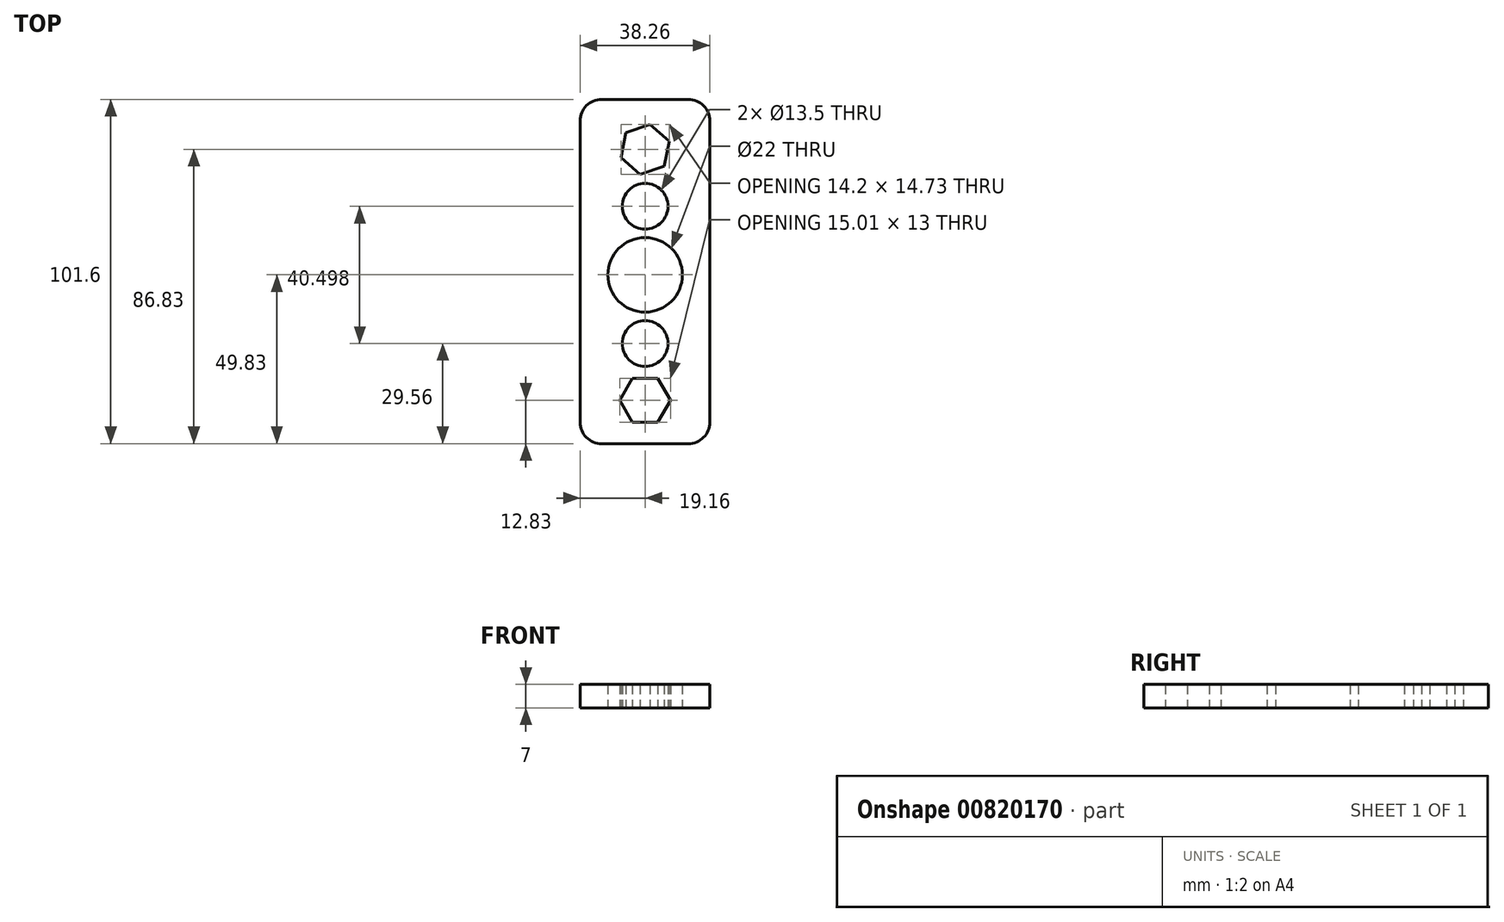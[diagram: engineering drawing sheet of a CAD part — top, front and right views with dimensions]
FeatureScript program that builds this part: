
annotation { "Feature Type Name" : "Feature", "Feature Type Description" : "" }
export const myFeature = defineFeature(function(context is Context, id is Id, definition is map)
    precondition{}
    {
        {
            var Q0;
            Q0=qCreatedBy(makeId("Top.planeOp"),FACE);
            var sketch = newSketch(context, id + "F0", { "sketchPlane" : qUnion([Q0])});
            skCircle(sketch, "E0", {"center": v(0, 0) * mm, "radius": 11 * mm});
            skLineSegment(sketch, "E1.bottom", {"start": v(-12.81, 51.77) * mm, "end": v(12.75, 51.77) * mm});
            skLineSegment(sketch, "E1.top", {"start": v(-12.81, -49.83) * mm, "end": v(12.75, -49.83) * mm});
            skLineSegment(sketch, "E1.left", {"start": v(-19.16, 45.42) * mm, "end": v(-19.16, -43.48) * mm});
            skLineSegment(sketch, "E1.right", {"start": v(19.1, 45.42) * mm, "end": v(19.1, -43.48) * mm});
            skPoint(sketch, "E2.visualSharp", {"position": v(-19.16, 51.77) * mm});
            skArc(sketch, "E2.filletArc", {"start": v(-12.81, 51.77) * mm, "mid": v(-17.3, 49.9) * mm, "end": v(-19.16, 45.42) * mm});
            skPoint(sketch, "E3.visualSharp", {"position": v(19.1, 51.77) * mm});
            skArc(sketch, "E3.filletArc", {"start": v(19.1, 45.42) * mm, "mid": v(17.24, 49.9) * mm, "end": v(12.75, 51.77) * mm});
            skPoint(sketch, "E4.visualSharp", {"position": v(19.1, -49.83) * mm});
            skArc(sketch, "E4.filletArc", {"start": v(12.75, -49.83) * mm, "mid": v(17.24, -47.97) * mm, "end": v(19.1, -43.48) * mm});
            skPoint(sketch, "E5.visualSharp", {"position": v(-19.16, -49.83) * mm});
            skArc(sketch, "E5.filletArc", {"start": v(-19.16, -43.48) * mm, "mid": v(-17.3, -47.97) * mm, "end": v(-12.81, -49.83) * mm});
            skCircle(sketch, "E6.cCircle", {"center": v(0, 37) * mm, "radius": 6.5 * mm, "construction": true});
            skLineSegment(sketch, "E6.0", {"start": v(7.1, 39.43) * mm, "end": v(5.66, 32.07) * mm});
            skLineSegment(sketch, "E6.1", {"start": v(5.66, 32.07) * mm, "end": v(-1.44, 29.63) * mm});
            skLineSegment(sketch, "E6.2", {"start": v(-1.44, 29.63) * mm, "end": v(-7.1, 34.57) * mm});
            skLineSegment(sketch, "E6.3", {"start": v(-7.1, 34.57) * mm, "end": v(-5.66, 41.93) * mm});
            skLineSegment(sketch, "E6.4", {"start": v(-5.66, 41.93) * mm, "end": v(1.44, 44.37) * mm});
            skLineSegment(sketch, "E6.5", {"start": v(1.44, 44.37) * mm, "end": v(7.1, 39.43) * mm});
            skPoint(sketch, "E6.0.midPoint", {"position": v(6.38, 35.75) * mm});
            skCircle(sketch, "E7.cCircle", {"center": v(0, -37) * mm, "radius": 6.5 * mm, "construction": true});
            skLineSegment(sketch, "E7.0", {"start": v(3.75, -43.5) * mm, "end": v(-3.75, -43.5) * mm});
            skLineSegment(sketch, "E7.1", {"start": v(-3.75, -43.5) * mm, "end": v(-7.5, -37) * mm});
            skLineSegment(sketch, "E7.2", {"start": v(-7.5, -37) * mm, "end": v(-3.75, -30.5) * mm});
            skLineSegment(sketch, "E7.3", {"start": v(-3.75, -30.5) * mm, "end": v(3.75, -30.5) * mm});
            skLineSegment(sketch, "E7.4", {"start": v(3.75, -30.5) * mm, "end": v(7.5, -37) * mm});
            skLineSegment(sketch, "E7.5", {"start": v(7.5, -37) * mm, "end": v(3.75, -43.5) * mm});
            skPoint(sketch, "E7.0.midPoint", {"position": v(0, -43.5) * mm});
            skCircle(sketch, "E8", {"center": v(0, -20.27) * mm, "radius": 6.75 * mm});
            skCircle(sketch, "E9", {"center": v(0, 20.23) * mm, "radius": 6.75 * mm});
            skSolve(sketch);
        }
        {
            var Q0;
            Q0 = qSketchRegion(id + "F0", true);
            extrude(context, id + "F1", {"entities" : qUnion([Q0]), "depth" : 7 * mm, "offsetDistance" : 25 * mm});
        }
    });
